# Revit family: Abmessungen emcoair KS
name_source: partatom
category: Air Terminals
revit_build: Autodesk Revit 2017 (Build: 20190508_0315(x64)
units: mm (PartAtom-declared; Revit-internal decimal feet)

## family parameters
Always vertical = Yes
Cut with Voids When Loaded = No
Part Type = Normal
Room Calculation Point = No
Round Connector Dimension = Use Diameter
Shared = No
Work Plane-Based = No

## types (4) — shared parameters
11_aktive Schlitzlänge Abluf = 600 mm
1_Tiefe = 370 mm  [stored 1.21391 ft]
2_Höhe, Frontblende = 170 mm  [stored 0.557743 ft]
4_Höhe Anschlusskasten, gesamt = 150 mm
6_Länge Zuluftstutzen / Abluftstutzen = 50 mm  [stored 0.164042 ft]
7_Durchmesser Zuluftstutzen / Abluftstutzen = 98 mm  [stored 0.321522 ft]
Product material = RAL 9016

## per-type parameters (varying)
| type | 3_Breite der Frontblende, gesamt | 5_Breite Anschlusskasten | 8_Abstand Mitte Zuluftstutzen / Mitte Abluftstutzen | Index |
| 550_3 | 550 mm | 517 mm  [stored 1.69619 ft] | 354 mm  [stored 1.16142 ft] | 1 |
| 750_3 | 750 mm  [stored 2.46063 ft] | 717 mm  [stored 2.35236 ft] | 554 mm  [stored 1.81759 ft] | 2 |
| 950_3 | 950 mm  [stored 3.1168 ft] | 917 mm  [stored 3.00853 ft] | 754 mm  [stored 2.47375 ft] | 3 |
| 1150_3 | 1150 mm | 1117 mm  [stored 3.6647 ft] | 954 mm  [stored 3.12992 ft] | 0 |

note: [stored X ft] marks values corroborated as IEEE doubles in the binary element streams (Revit-internal decimal feet)

## geometry (parser evidence)
native form markers: Sweep x2
no freeform markers — native parametric forms only
